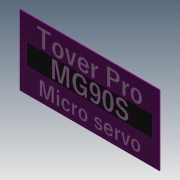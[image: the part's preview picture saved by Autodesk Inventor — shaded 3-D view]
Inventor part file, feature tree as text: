
AUTODESK INVENTOR PART (.ipt)
format: ipt  version: 2017 (Build 210142000, 142)  size: 784,896 bytes
history: native  units: mm
features: other x3, sketch x3, extrude x1
ambient origin geometry x8: Origin, YZ Plane, XZ Plane, XY Plane, X Axis, Y Axis, Z Axis, Center Point
bodies: Body1 (feature_tree)
feature tree (7):
  other  "Твердое тело1"
  extrude  "Выдавливание1"  Depth=20.0mm
  other  "Рельеф1"
  other  "Рельеф2"
  sketch  "Эскиз1"
  sketch  "Эскиз2"
  sketch  "Эскиз3"
